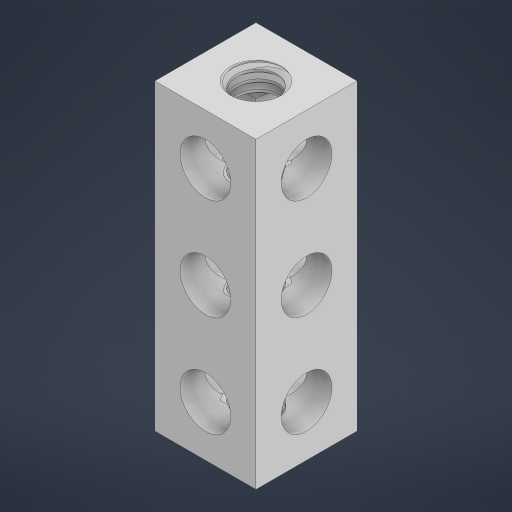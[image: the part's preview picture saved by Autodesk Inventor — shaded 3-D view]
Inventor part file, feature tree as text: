
AUTODESK INVENTOR PART (.ipt)
format: ipt  version: 2023 (Build 270158000, 158)  size: 1,501,696 bytes
history: native  units: in
note: dims shown in document units (in); Inventor stores cm internally (conversion verified against a paired STEP export)
features: mirror x1
ambient origin geometry x8: Origin, YZ Plane, XZ Plane, XY Plane, X Axis, Y Axis, Z Axis, Center Point
bodies: Solid1 (feature_tree)
feature tree (1):
  mirror  "Mirror3"
